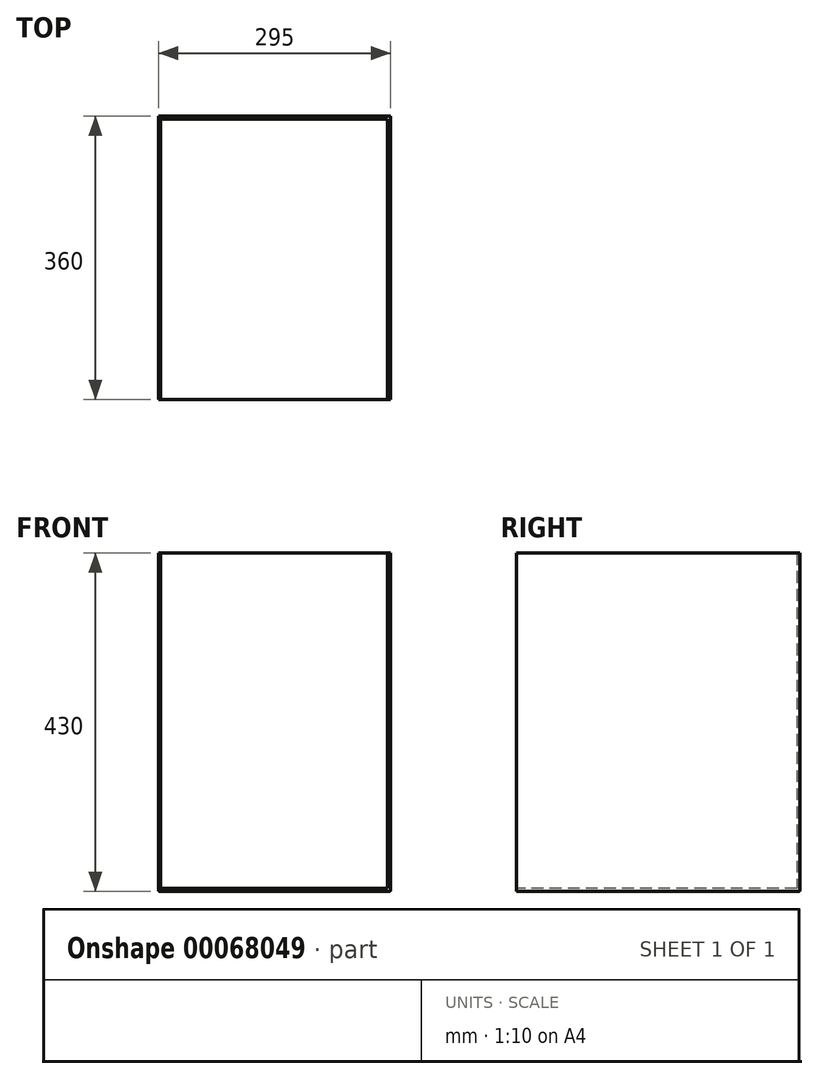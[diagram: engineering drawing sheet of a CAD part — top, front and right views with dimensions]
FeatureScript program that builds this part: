
annotation { "Feature Type Name" : "Feature", "Feature Type Description" : "" }
export const myFeature = defineFeature(function(context is Context, id is Id, definition is map)
    precondition{}
    {
        {
            var Q0;
            Q0=qCreatedBy(makeId("Top.planeOp"),FACE);
            var sketch = newSketch(context, id + "F0", { "sketchPlane" : qUnion([Q0])});
            skLineSegment(sketch, "E0", {"start": v(0, -360) * mm, "end": v(0, 0) * mm});
            skLineSegment(sketch, "E1.MirrorCS", {"start": v(-4, -360) * mm, "end": v(-4, -4) * mm});
            skLineSegment(sketch, "E2.MirrorCS", {"start": v(-4, -4) * mm, "end": v(-292.18, -4) * mm});
            skLineSegment(sketch, "E3.MirrorCS", {"start": v(0, 0) * mm, "end": v(-295, 0) * mm});
            skLineSegment(sketch, "E4.MirrorCS", {"start": v(-295, 0) * mm, "end": v(-295, -360) * mm});
            skLineSegment(sketch, "E5.MirrorCS", {"start": v(-292.18, -4) * mm, "end": v(-292.18, -360) * mm});
            skLineSegment(sketch, "E6.MirrorCS", {"start": v(-292.18, -360) * mm, "end": v(-295, -360) * mm});
            skLineSegment(sketch, "E7", {"start": v(0, -360) * mm, "end": v(-4, -360) * mm});
            skSolve(sketch);
        }
        {
            var Q0;
            Q0=makeQuery(id+"F0.imprint","IMPRINT",FACE,{"disambiguationData":[TD([[makeQuery(id+"F0.imprint","IMPRINT",EDGE,{"derivedFrom":sQuery(id+"F0.wireOp",EDGE,"8549452f-c1c4-4c66-b43a-6f4cb653c117")}),-1.0]])]});
            var Q1;
            Q1=makeQuery(id+"F0.imprint","IMPRINT",FACE,{"disambiguationData":[TD([[makeQuery(id+"F0.imprint","IMPRINT",EDGE,{"derivedFrom":sQuery(id+"F0.wireOp",EDGE,"E0")}),1.0]])]});
            extrude(context, id + "F1", {"entities" : qUnion([Q0, Q1]), "depth" : 426 * mm});
        }
        {
            var Q0;
            Q0=qCreatedBy(makeId("Top.planeOp"),FACE);
            var sketch = newSketch(context, id + "F2", { "sketchPlane" : qUnion([Q0])});
            skLineSegment(sketch, "E8.0", {"start": v(-295, 0) * mm, "end": v(-295, -360) * mm});
            skLineSegment(sketch, "E9.0", {"start": v(0, 0) * mm, "end": v(-295, 0) * mm});
            skLineSegment(sketch, "E10", {"start": v(-295, -360) * mm, "end": v(0, -360) * mm});
            skLineSegment(sketch, "E11", {"start": v(0, -360) * mm, "end": v(0, 0) * mm});
            skSolve(sketch);
        }
        {
            var Q0;
            Q0=qSketchRegion(id+"F2",true);
            extrude(context, id + "F3", {"entities" : qUnion([Q0]), "operationType" : NewBodyOperationType.ADD, "oppositeDirection" : true, "depth" : 4 * mm});
        }
        {
            var Q0;
            Q0=makeQuery(id+"F3.opExtrude","CAP_EDGE",EDGE,{"disambiguationData":[OSD([sQuery(id+"F2.wireOp",EDGE,"E11")])],"isStart":false});
            var Q1;
            Q1=makeQuery(id+"F3.opExtrude","CAP_EDGE",EDGE,{"disambiguationData":[OSD([sQuery(id+"F2.wireOp",EDGE,"E8.0")])],"isStart":false});
            var Q2;
            Q2=makeQuery(id+"F3.opExtrude","CAP_EDGE",EDGE,{"disambiguationData":[OSD([sQuery(id+"F2.wireOp",EDGE,"E9.0")])],"isStart":false});
            fillet(context, id + "F4", {"entities" : qUnion([Q0, Q1, Q2]), "radius" : 2 * mm, "tangentPropagation" : true, "allowEdgeOverflow" : false});
        }
    });
